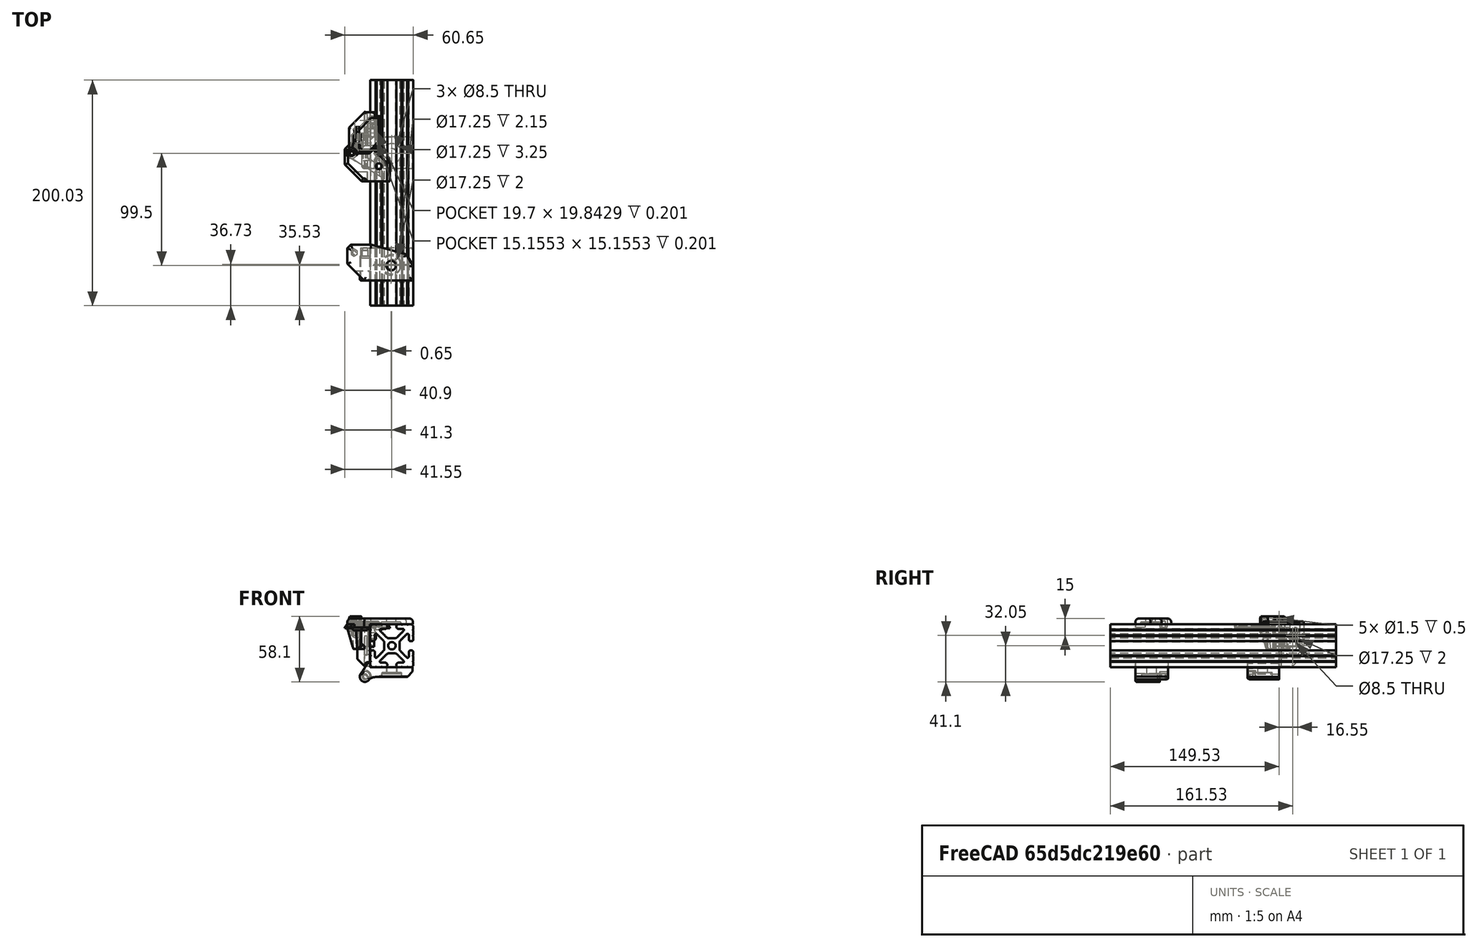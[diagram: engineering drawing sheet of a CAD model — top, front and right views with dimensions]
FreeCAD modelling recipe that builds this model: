
FCSTD DOCUMENT  (FreeCAD 0.18R)
Label: rambo-upper-mount
License: All rights reserved
LicenseURL: http://en.wikipedia.org/wiki/All_rights_reserved
objects: Sketcher::SketchObject×17, PartDesign::Fillet×9, PartDesign::Pad×8, PartDesign::Pocket×7, Part::Feature×6, PartDesign::Body×3, Mesh::Feature×2, PartDesign::Revolution×2, PartDesign::Chamfer×1
note: 70 computed .brp shape members not serialized (recipe doc carries the construction recipe); baked Part::Feature solids carry a one-line shape summary decoded from their .brp

FEATURE [Sketcher::SketchObject] Sketch
  MapMode = 5
  Support = -> [XY_Plane]
  sketch-geometry (7):
    g0: LineSegment StartX=-2.25 StartY=22.75 StartZ=0 EndX=-2.25 EndY=4.5 EndZ=0
    g1: LineSegment StartX=-2.25 StartY=4.5 StartZ=0 EndX=2.25 EndY=0 EndZ=0
    g2: LineSegment StartX=2.25 StartY=0 StartZ=0 EndX=15.7 EndY=0 EndZ=0
    g3: LineSegment StartX=15.7 StartY=0 StartZ=0 EndX=20.5 EndY=4.8 EndZ=0
    g4: LineSegment StartX=20.5 StartY=36.5 StartZ=0 EndX=20.5 EndY=4.8 EndZ=0
    g5: LineSegment StartX=11.5 StartY=36.5 StartZ=0 EndX=20.5 EndY=36.5 EndZ=0
    g6: LineSegment StartX=11.5 StartY=36.5 StartZ=0 EndX=-2.25 EndY=22.75 EndZ=0
  constraints (21):
    c: Coincident(g1,g0)
    c: PointOnObject(g1,g-1)
    c: Coincident(g2,g1)
    c: Horizontal(g2)
    c: Coincident(g4,g3)
    c: Vertical(g4)
    c: Coincident(g5,g4)
    c: Horizontal(g5)
    c: Coincident(g6,g5)
    c: Coincident(g6,g0)
    c: Angle(g1,g0) = 2.35619
    c: Angle(g0,g6) = 2.35619
    c: Angle(g3,g2) = 2.35619
    c: DistanceX(g-1,g5) = 11.5
    c: DistanceY(g-1,g5) = 36.5
    c: DistanceX(g5,g5) = 9
    c: Coincident(g3,g2)
    c: DistanceX(g-1,g2) = 15.7
    c: DistanceX(g-1,g1) = 2.25
    c: Vertical(g0)
    c: DistanceX(g0,g-1) = 2.25
FEATURE [Part::Feature] rambo_base_upper_mount
  shape: bbox 25.4 x 33.05 x 22.5 mm, 98 faces (baked)
  expr: Placement.Base.z = 0
FEATURE [Part::Feature] rambo_base_lower_mount
  shape: bbox 39.91 x 31.71 x 6.307 mm, 79 faces (baked)
FEATURE [Part::Feature] rambo_lid_lower_hinge
  shape: bbox 15.91 x 28.51 x 29.3 mm, 59 faces (baked)
FEATURE [Part::Feature] rambo_base_upper_mount_cs
  shape: bbox 20 x 29.18 x 3e-07 mm, 0 faces, 0 solids (baked)
FEATURE [PartDesign::Pad] Pad
  Length = 2.5
  Length2 = 100
  Profile = -> Sketch
  Type = 0
FEATURE [Sketcher::SketchObject] Sketch001
  AttachmentOffset = pos=(0,0,-14.5) rot=(0,0,1;0rad)
  MapMode = 5
  Placement = pos=(0,14.5,3.2e-15) rot=(1,0,0;1.5708rad)
  Support = -> [XZ_Plane]
  sketch-geometry (5):
    g0: LineSegment StartX=5 StartY=0 StartZ=0 EndX=5 EndY=-30.75 EndZ=0
    g1: LineSegment StartX=5 StartY=-30.75 StartZ=0 EndX=11.25 EndY=-37 EndZ=0
    g2: LineSegment StartX=11.25 StartY=-37 StartZ=0 EndX=16.25 EndY=-37 EndZ=0
    g3: LineSegment StartX=16.25 StartY=-37 StartZ=0 EndX=16.25 EndY=0 EndZ=0
    g4: LineSegment StartX=16.25 StartY=0 StartZ=0 EndX=5 EndY=0 EndZ=0
  constraints (15):
    c: Horizontal(g2)
    c: PointOnObject(g3,g-1)
    c: Vertical(g3)
    c: Angle(g1,g0) = 2.35619
    c: Coincident(g1,g2)
    c: Coincident(g0,g1)
    c: Coincident(g3,g2)
    c: Coincident(g4,g3)
    c: Vertical(g0)
    c: Coincident(g4,g0)
    c: Horizontal(g4)
    c: DistanceX(g-1,g0) = 5
    c: DistanceX(g-1,g3) = 16.25
    c: DistanceY(g2,g-1) = 37
    c: DistanceX(g2,g2) = 5
FEATURE [PartDesign::Pad] Pad001
  BaseFeature = -> Pad
  Length = 2
  Length2 = 100
  Profile = -> Sketch001
  Reversed = true
  Type = 0
FEATURE [Sketcher::SketchObject] Sketch002
  AttachmentOffset = pos=(0,0,16.5) rot=(0,0,1;0rad)
  MapMode = 5
  Placement = pos=(16.5,-3.7e-15,3.7e-15) rot=(0.57735,0.57735,0.57735;2.0944rad)
  Support = -> [YZ_Plane]
  sketch-geometry (6):
    g0: LineSegment StartX=16.5 StartY=0 StartZ=0 EndX=36.5 EndY=0 EndZ=0
    g1: LineSegment StartX=16.5 StartY=0 StartZ=0 EndX=16.5 EndY=-37 EndZ=0
    g2: LineSegment StartX=16.5 StartY=-37 StartZ=0 EndX=26.5 EndY=-37 EndZ=0
    g3: LineSegment StartX=36.5 StartY=0 StartZ=0 EndX=36.5 EndY=-27 EndZ=0
    g4: Circle CenterX=26.5 CenterY=-19.05 CenterZ=0 NormalX=0 NormalY=0 NormalZ=1 AngleXU=0 Radius=4.25
    g5: LineSegment StartX=26.5 StartY=-37 StartZ=0 EndX=36.5 EndY=-27 EndZ=0
  constraints (18):
    c: Coincident(g1,g0)
    c: Vertical(g1)
    c: Horizontal(g2)
    c: DistanceX(g-1,g0) = 16.5
    c: DistanceY(g2,g-1) = 37
    c: Coincident(g2,g1)
    c: Vertical(g3)
    c: Diameter(g4) = 8.5
    c: DistanceY(g4,g-1) = 19.05
    c: Horizontal(g0)
    c: DistanceY(g-1,g0) = 0
    c: DistanceX(g0,g4) = 10
    c: DistanceX(g0,g3) = 20
    c: Coincident(g5,g2)
    c: DistanceX(g2,g5) = 10
    c: Coincident(g5,g3)
    c: Angle(g3,g5) = 2.35619
    c: Coincident(g3,g0)
FEATURE [PartDesign::Pad] Pad002
  BaseFeature = -> Pad001
  Length = 5
  Length2 = 100
  Profile = -> Sketch002
  Reversed = true
  Type = 0
FEATURE [Sketcher::SketchObject] Sketch003
  AttachmentOffset = pos=(0,0,11.5) rot=(0,0,1;0rad)
  MapMode = 5
  Placement = pos=(11.5,-2.6e-15,2.6e-15) rot=(0.57735,0.57735,0.57735;2.0944rad)
  Support = -> [YZ_Plane]
  sketch-geometry (1):
    g0: Circle CenterX=26.5 CenterY=-19.05 CenterZ=0 NormalX=0 NormalY=0 NormalZ=1 AngleXU=0 Radius=8.625
  constraints (3):
    c: Diameter(g0) = 17.25
    c: DistanceY(g0,g-1) = 19.05
    c: DistanceX(g-1,g0) = 26.5
FEATURE [PartDesign::Pocket] Pocket
  BaseFeature = -> Pad002
  Length = 2
  Length2 = 100
  Profile = -> Sketch003
  Reversed = true
  Type = 0
FEATURE [Sketcher::SketchObject] Sketch004
  MapMode = 5
  Support = -> [XY_Plane]
  sketch-geometry (7):
    g0: LineSegment StartX=2.25 StartY=3 StartZ=0 EndX=5.7141 EndY=5 EndZ=0
    g1: LineSegment StartX=5.7141 StartY=5 StartZ=0 EndX=5.7141 EndY=9 EndZ=0
    g2: LineSegment StartX=5.7141 StartY=9 StartZ=0 EndX=2.25 EndY=11 EndZ=0
    g3: LineSegment StartX=2.25 StartY=11 StartZ=0 EndX=-1.2141 EndY=9 EndZ=0
    g4: LineSegment StartX=-1.2141 StartY=9 StartZ=0 EndX=-1.2141 EndY=5 EndZ=0
    g5: LineSegment StartX=-1.2141 StartY=5 StartZ=0 EndX=2.25 EndY=3 EndZ=0
    g6: Circle [constr] CenterX=2.25 CenterY=7 CenterZ=0 NormalX=0 NormalY=0 NormalZ=1 AngleXU=0 Radius=4
  constraints (17):
    c: Coincident(g0,g1)
    c: Coincident(g1,g2)
    c: Coincident(g2,g3)
    c: Coincident(g3,g4)
    c: Coincident(g4,g5)
    c: Coincident(g5,g0)
    c: Equal(g0, g1-g5) x5
    c: PointOnObject(g0,g6)
    c: PointOnObject(g1,g6)
    c: PointOnObject(g2,g6)
    c: PointOnObject(g3,g6)
    c: PointOnObject(g4,g6)
    c: PointOnObject(g5,g6)
    c: DistanceX(g-1,g6) = 2.25
    c: DistanceY(g-1,g6) = 7
    c: Vertical(g1)
    c: DistanceY(g0,g6) = 4
FEATURE [PartDesign::Pad] Pad003
  BaseFeature = -> Pocket
  Length = 3
  Length2 = 100
  Profile = -> Sketch004
  Reversed = true
  Type = 0
FEATURE [Sketcher::SketchObject] Sketch005
  AttachmentOffset = pos=(0,0,-3) rot=(0,0,1;0rad)
  MapMode = 5
  Placement = pos=(0,0,-3) rot=(0,0,1;0rad)
  Support = -> [XY_Plane]
  sketch-geometry (1):
    g0: Circle CenterX=2.25 CenterY=7 CenterZ=0 NormalX=0 NormalY=0 NormalZ=1 AngleXU=0 Radius=1.5
  constraints (3):
    c: Diameter(g0) = 3
    c: DistanceX(g-1,g0) = 2.25
    c: DistanceY(g-1,g0) = 7
FEATURE [PartDesign::Pocket] Pocket001
  BaseFeature = -> Pad003
  Length = 5
  Length2 = 100
  Midplane = true
  Profile = -> Sketch005
  Type = 1
FEATURE [Part::Feature] _515_extrusion_200_25mm_7_7_8in
  Placement = pos=(-110.45,65,-76.25) rot=(1,0,0;1.5708rad)
  shape: bbox 38.1 x 200 x 38.1 mm, 113 faces (baked)
FEATURE [Mesh::Feature] Einsy_base  label="Einsy-base"
  Placement = pos=(16.25,14.5,0) rot=(-0.707107,0.707107,0;3.14159rad)
FEATURE [Part::Feature] rambo_lower_mount
  Placement = pos=(2.25,-88,0) rot=(0,0,1;0rad)
  shape: bbox 58.05 x 31.7 x 8 mm, 46 faces (baked)
FEATURE [PartDesign::Fillet] Fillet
  Base = -> Pocket001 [Face5]
  BaseFeature = -> Pocket001
  Radius = 1.3
FEATURE [PartDesign::Fillet] Fillet001
  Base = -> Fillet [Edge44,Edge46,Edge45]
  BaseFeature = -> Fillet
  Radius = 1
FEATURE [PartDesign::Fillet] Fillet002
  Base = -> Fillet001 [Edge65,Edge102]
  BaseFeature = -> Fillet001
  Radius = 1
FEATURE [PartDesign::Fillet] Fillet003
  Base = -> Fillet002 [Edge83,Edge73,Edge75,Edge77,Edge79,Edge81]
  BaseFeature = -> Fillet002
  Radius = 0.25
FEATURE [PartDesign::Fillet] Fillet004
  Base = -> Fillet003 [Edge40]
  BaseFeature = -> Fillet003
  Radius = 0.35
FEATURE [PartDesign::Body] Body  label="rambo-upper-mount"
  Group = -> [Sketch,Pad,Sketch001,Pad001,Sketch002,Pad002,Sketch003,Pocket,Sketch004,Pad003,Sketch005,Pocket001,Fillet,Fillet001,Fillet002,Fillet003,Fillet004]
  Origin = -> Origin
  Tip = -> Fillet004
FEATURE [Mesh::Feature] Einsy_doors  label="Einsy-doors"
  Placement = pos=(-75.75,14.5,-51) rot=(0,0,1;4.71239rad)
FEATURE [Sketcher::SketchObject] Sketch006
  MapMode = 5
  Support = -> [XY_Plane001]
  sketch-geometry (10):
    g0: LineSegment StartX=0.5 StartY=0.25 StartZ=0 EndX=37.5 EndY=0.25 EndZ=0
    g1: LineSegment StartX=37.5 StartY=0.25 StartZ=0 EndX=37.5 EndY=4.25 EndZ=0
    g2: LineSegment StartX=33.5 StartY=8.5 StartZ=0 EndX=37.5 EndY=4.25 EndZ=0
    g3: LineSegment StartX=-8.36135 StartY=6 StartZ=0 EndX=-1.5 EndY=-4.23326 EndZ=0
    g4: LineSegment StartX=-1 StartY=-4.5 StartZ=0 EndX=0.25 EndY=-4.5 EndZ=0
    g5: LineSegment StartX=33.5 StartY=8.5 StartZ=0 EndX=0.1 EndY=8.5 EndZ=0
    g6: LineSegment StartX=0.25 StartY=-4.5 StartZ=0 EndX=0.25 EndY=0 EndZ=0
    g7: ArcOfCircle CenterX=0.5 CenterY=0 CenterZ=0 NormalX=0 NormalY=0 NormalZ=1 AngleXU=0 Radius=0.25 StartAngle=1.5708 EndAngle=3.14159
    g8: ArcOfCircle CenterX=-4.5 CenterY=8.5 CenterZ=0 NormalX=0 NormalY=0 NormalZ=1 AngleXU=0 Radius=4.6 StartAngle=3.71617 EndAngle=6.28319
    g9: ArcOfCircle CenterX=-1 CenterY=-3.89801 CenterZ=0 NormalX=0 NormalY=0 NormalZ=1 AngleXU=0 Radius=0.601989 StartAngle=3.73224 EndAngle=4.71239
  constraints (29):
    c: Horizontal(g0)
    c: Coincident(g1,g0)
    c: Vertical(g1)
    c: DistanceY(g0,g1) = 4
    c: Coincident(g2,g1)
    c: Horizontal(g5)
    c: Coincident(g5,g2)
    c: DistanceX(g2,g1) = 4
    c: Horizontal(g4)
    c: DistanceX(g-1,g4) = 0.25
    c: Coincident(g6,g4)
    c: Vertical(g6)
    c: Tangent(g0,g7) = 1.5708
    c: Tangent(g6,g7) = 1.5708
    c: DistanceX(g6,g7) = 0.25
    c: PointOnObject(g7,g-1)
    c: Diameter(g8) = 9.2
    c: DistanceX(g8,g-1) = 4.5
    c: DistanceY(g-1,g8) = 8.5
    c: DistanceX(g0,g0) = 37
    c: DistanceY(g6,g6) = 4.5
    c: Tangent(g3,g9) = -1.5708
    c: Tangent(g4,g9) = -1.5708
    c: DistanceX(g3,g9) = 0.5
    c: DistanceX(g4,g4) = 1.25
    c: Coincident(g8,g3)
    c: Coincident(g8,g5)
    c: DistanceY(g-1,g3) = 6
    c: DistanceY(g-1,g5) = 8.5
FEATURE [PartDesign::Pad] Pad004
  Length = 29
  Length2 = 100
  Profile = -> Sketch006
  Reversed = true
  Type = 0
FEATURE [Sketcher::SketchObject] Sketch007
  AttachmentOffset = pos=(-4.5,-9.3,-8.49) rot=(0,1,0;-4.71239rad)
  MapMode = 5
  Placement = pos=(-4.5,8.49,-9.3) rot=(0.57735,0.57735,0.57735;2.0944rad)
  Support = -> [XZ_Plane001]
  sketch-geometry (8):
    g0: LineSegment StartX=-1.75 StartY=9.3 StartZ=0 EndX=0 EndY=9.3 EndZ=0
    g1: LineSegment StartX=-1.75 StartY=9.3 StartZ=0 EndX=-2.5 EndY=7.15 EndZ=0
    g2: LineSegment StartX=-2.5 StartY=7.15 StartZ=0 EndX=-2.5 EndY=2 EndZ=0
    g3: LineSegment StartX=0 StartY=0 StartZ=0 EndX=0 EndY=9.3 EndZ=0
    g4: LineSegment StartX=-2.5 StartY=2 StartZ=0 EndX=-4.6 EndY=2 EndZ=0
    g5: LineSegment StartX=-4.6 StartY=2 StartZ=0 EndX=-4.6 EndY=0 EndZ=0
    g6: LineSegment StartX=-4.6 StartY=0 StartZ=0 EndX=0 EndY=0 EndZ=0
    g7: LineSegment StartX=0 StartY=9.3 StartZ=0 EndX=0 EndY=0 EndZ=0
  constraints (23):
    c: Horizontal(g0)
    c: Coincident(g2,g1)
    c: Vertical(g2)
    c: Coincident(g3,g0)
    c: Vertical(g3)
    c: Coincident(g0,g1)
    c: DistanceX(g0,g0) = 1.75
    c: PointOnObject(g3,g-2)
    c: DistanceX(g1,g3) = 2.5
    c: DistanceY(g1,g0) = 2.15
    c: DistanceY(g2,g1) = 5.15
    c: Coincident(g4,g2)
    c: Horizontal(g4)
    c: DistanceX(g4,g2) = 2.1
    c: Coincident(g5,g4)
    c: PointOnObject(g5,g-1)
    c: Vertical(g5)
    c: Coincident(g6,g5)
    c: Horizontal(g6)
    c: DistanceY(g5,g4) = 2
    c: Coincident(g7,g0)
    c: Coincident(g7,g6)
    c: Coincident(g3,g6)
FEATURE [PartDesign::Revolution] Revolution
  Angle = 360
  Axis = (0,-2e-16,1)
  Base = (-4.5,8.49,-9.3)
  BaseFeature = -> Pad004
  Midplane = true
  Profile = -> Sketch007
  ReferenceAxis = -> Sketch007 [V_Axis]
  Refine = true
FEATURE [Sketcher::SketchObject] Sketch008
  AttachmentOffset = pos=(0,0,-29) rot=(0,0,1;0rad)
  MapMode = 5
  Placement = pos=(0,0,-29) rot=(0,0,1;0rad)
  Support = -> [XY_Plane001]
  sketch-geometry (1):
    g0: Circle CenterX=-4.5 CenterY=8.5 CenterZ=0 NormalX=0 NormalY=0 NormalZ=1 AngleXU=0 Radius=4.6
  constraints (3):
    c: Diameter(g0) = 9.2
    c: DistanceX(g0,g-1) = 4.5
    c: DistanceY(g-1,g0) = 8.5
FEATURE [PartDesign::Pad] Pad005
  BaseFeature = -> Revolution
  Length = 19.7
  Length2 = 100
  Profile = -> Sketch008
  Type = 0
FEATURE [Sketcher::SketchObject] Sketch009
  MapMode = 5
  Support = -> [XY_Plane001]
  sketch-geometry (9):
    g0: ArcOfCircle CenterX=-4.5 CenterY=8.5 CenterZ=0 NormalX=0 NormalY=0 NormalZ=1 AngleXU=0 Radius=4.6 StartAngle=0 EndAngle=0.511093
    g1: Circle [constr] CenterX=-0.487831 CenterY=10.75 CenterZ=0 NormalX=0 NormalY=0 NormalZ=1 AngleXU=0 Radius=0.8
    g2: Circle [constr] CenterX=1.778 CenterY=8.5 CenterZ=0 NormalX=0 NormalY=0 NormalZ=1 AngleXU=0 Radius=0.8
    g3: Circle [constr] CenterX=9.875 CenterY=8.5 CenterZ=0 NormalX=0 NormalY=0 NormalZ=1 AngleXU=0 Radius=0.8
    g4: BSplineCurve PolesCount=3 KnotsCount=2 Degree=2 IsPeriodic=0
    g5: GeomPoint [constr] X=-0.487831 Y=10.75 Z=0
    g6: GeomPoint [constr] X=9.875 Y=8.5 Z=0
    g7: LineSegment StartX=0.1 StartY=8.5 StartZ=0 EndX=1.778 EndY=8.5 EndZ=0
    g8: LineSegment StartX=1.778 StartY=8.5 StartZ=0 EndX=9.875 EndY=8.5 EndZ=0
  constraints (21):
    c: Diameter(g0) = 9.2
    c: DistanceX(g0,g-1) = 4.5
    c: DistanceY(g-1,g0) = 8.5
    c: Radius(g1) = 0.8
    c: Equal(g1,g2)
    c: Equal(g1,g3)
    c: InternalAlignment(g1,g4)
    c: InternalAlignment(g2,g4)
    c: InternalAlignment(g3,g4)
    c: InternalAlignment(g5,g4)
    c: InternalAlignment(g6,g4)
    c: DistanceX(g-1,g4) = 9.875
    c: DistanceY(g4,g2) = 0
    c: Horizontal(g7)
    c: Coincident(g7,g2)
    c: Coincident(g0,g7)
    c: Coincident(g0,g4)
    c: DistanceY(g-1,g4) = 8.5
    c: DistanceY(g0,g0) = 2.25
    c: Coincident(g8,g4)
    c: Horizontal(g8)
FEATURE [PartDesign::Pad] Pad006
  BaseFeature = -> Pad005
  Length = 29
  Length2 = 100
  Profile = -> Sketch009
  Reversed = true
  Type = 0
FEATURE [Sketcher::SketchObject] Sketch010
  MapMode = 5
  Placement = pos=(0,0,0) rot=(1,0,0;1.5708rad)
  Support = -> [XZ_Plane001]
  sketch-geometry (1):
    g0: Circle CenterX=19.05 CenterY=-14.5 CenterZ=0 NormalX=0 NormalY=0 NormalZ=1 AngleXU=0 Radius=4.25
  constraints (3):
    c: Diameter(g0) = 8.5
    c: DistanceX(g-1,g0) = 19.05
    c: DistanceY(g0,g-1) = 14.5
FEATURE [PartDesign::Pocket] Pocket002
  BaseFeature = -> Pad006
  Length = 5
  Length2 = 100
  Profile = -> Sketch010
  Type = 1
FEATURE [Sketcher::SketchObject] Sketch011
  AttachmentOffset = pos=(0,0,-6) rot=(0,0,1;0rad)
  MapMode = 5
  Placement = pos=(0,6,1.3e-15) rot=(1,0,0;1.5708rad)
  Support = -> [XZ_Plane001]
  sketch-geometry (1):
    g0: Circle CenterX=19.05 CenterY=-14.5 CenterZ=0 NormalX=0 NormalY=0 NormalZ=1 AngleXU=0 Radius=8.625
  constraints (3):
    c: Diameter(g0) = 17.25
    c: DistanceX(g-1,g0) = 19.05
    c: DistanceY(g0,g-1) = 14.5
FEATURE [PartDesign::Pocket] Pocket003
  BaseFeature = -> Pocket002
  Length = 5
  Length2 = 100
  Profile = -> Sketch011
  Type = 0
FEATURE [PartDesign::Fillet] Fillet005
  Base = -> Pocket003 [Edge33,Edge58,Edge28,Edge52,Edge27,Edge26,Edge51,Edge15,Edge14,Edge16,Edge56]
  BaseFeature = -> Pocket003
  Radius = 1.3
FEATURE [PartDesign::Fillet] Fillet006
  Base = -> Fillet005 [Edge109]
  BaseFeature = -> Fillet005
  Radius = 0.35
FEATURE [PartDesign::Body] Body001  label="rambo-lower-hinge"
  Group = -> [Sketch006,Pad004,Sketch007,Revolution,Sketch008,Pad005,Sketch009,Pad006,Sketch010,Pocket002,Sketch011,Pocket003,Fillet005,Fillet006]
  Origin = -> Origin001
  Placement = pos=(16.25,-83.8,-38) rot=(-1,0,0;1.5708rad)
  Tip = -> Fillet006
FEATURE [Sketcher::SketchObject] Sketch012
  AttachmentOffset = pos=(16,14.5,-38.1) rot=(1,0,0;-1.5708rad)
  MapMode = 5
  Placement = pos=(16,14.5,-38.1) rot=(1,0,0;4.71239rad)
  Support = -> [XY_Plane002]
  sketch-geometry (11):
    g0: LineSegment StartX=0.5 StartY=0.25 StartZ=0 EndX=37.5 EndY=0.25 EndZ=0
    g1: LineSegment StartX=37.5 StartY=0.25 StartZ=0 EndX=37.5 EndY=4.25 EndZ=0
    g2: LineSegment StartX=33.5 StartY=8.5 StartZ=0 EndX=37.5 EndY=4.25 EndZ=0
    g3: LineSegment StartX=-2.71273 StartY=-4.5 StartZ=0 EndX=0.25 EndY=-4.5 EndZ=0
    g4: LineSegment StartX=33.5 StartY=8.5 StartZ=0 EndX=-1.752 EndY=8.5 EndZ=0
    g5: LineSegment StartX=0.25 StartY=-4.5 StartZ=0 EndX=0.25 EndY=0 EndZ=0
    g6: ArcOfCircle CenterX=0.5 CenterY=0 CenterZ=0 NormalX=0 NormalY=0 NormalZ=1 AngleXU=0 Radius=0.25 StartAngle=1.5708 EndAngle=3.14159
    g7: LineSegment StartX=-5.87481 StartY=6.5 StartZ=0 EndX=-4.064 EndY=1.4 EndZ=0
    g8: LineSegment StartX=-4.064 StartY=1.4 StartZ=0 EndX=-4.064 EndY=-3.14873 EndZ=0
    g9: LineSegment StartX=-4.064 StartY=-3.14873 StartZ=0 EndX=-2.71273 EndY=-4.5 EndZ=0
    g10: ArcOfCircle CenterX=-4.25 CenterY=8.4 CenterZ=0 NormalX=0 NormalY=0 NormalZ=1 AngleXU=0 Radius=2.5 StartAngle=0.0400107 EndAngle=4.00491
  constraints (28):
    c: Horizontal(g0)
    c: Coincident(g1,g0)
    c: Vertical(g1)
    c: DistanceY(g0,g1) = 4
    c: Coincident(g2,g1)
    c: Horizontal(g4)
    c: Coincident(g4,g2)
    c: DistanceX(g2,g1) = 4
    c: Horizontal(g3)
    c: Coincident(g5,g3)
    c: Vertical(g5)
    c: Tangent(g0,g6) = 1.5708
    c: Tangent(g5,g6) = 1.5708
    c: DistanceX(g5,g6) = 0.25
    c: PointOnObject(g6,g-1)
    c: DistanceX(g0,g0) = 37
    c: DistanceY(g5,g5) = 4.5
    c: Vertical(g8)
    c: Coincident(g9,g3)
    c: Coincident(g9,g8)
    c: Coincident(g8,g7)
    c: Angle(g9,g8) = 2.35619
    c: Diameter(g10) = 5
    c: DistanceX(g10,g-1) = 4.25
    c: DistanceY(g-1,g10) = 8.4
    c: DistanceY(g-1,g7) = 1.4
    c: Coincident(g10,g4)
    c: Coincident(g10,g7)
FEATURE [PartDesign::Pad] Pad007
  Length = 28
  Length2 = 100
  Profile = -> Sketch012
  Reversed = true
  Type = 0
FEATURE [Sketcher::SketchObject] Sketch013
  AttachmentOffset = pos=(0,0,6.5) rot=(0,0,1;0rad)
  MapMode = 5
  Placement = pos=(0,-6.5,-1.4e-15) rot=(1,0,0;1.5708rad)
  Support = -> [XZ_Plane002]
  sketch-geometry (1):
    g0: Circle CenterX=11.75 CenterY=-46.5 CenterZ=0 NormalX=0 NormalY=0 NormalZ=1 AngleXU=0 Radius=4.625
  constraints (3):
    c: Diameter(g0) = 9.25
    c: DistanceX(g-1,g0) = 11.75
    c: DistanceY(g0,g-1) = 46.5
FEATURE [PartDesign::Pocket] Pocket004
  BaseFeature = -> Pad007
  Length = 7
  Length2 = 100
  Profile = -> Sketch013
  Reversed = true
  Type = 0
FEATURE [Sketcher::SketchObject] Sketch014
  AttachmentOffset = pos=(-6.5,-46.5,11.75) rot=(0,0,1;0rad)
  MapMode = 5
  Placement = pos=(11.75,-6.5,-46.5) rot=(0.57735,0.57735,0.57735;2.0944rad)
  Support = -> [YZ_Plane002]
  sketch-geometry (5):
    g0: LineSegment StartX=-6.73205 StartY=1.5 StartZ=0 EndX=-6.73205 EndY=0 EndZ=0
    g1: LineSegment StartX=-5 StartY=2.5 StartZ=0 EndX=0 EndY=2.5 EndZ=0
    g2: LineSegment StartX=0 StartY=2.5 StartZ=0 EndX=0 EndY=0 EndZ=0
    g3: LineSegment StartX=-6.73205 StartY=0 StartZ=0 EndX=0 EndY=0 EndZ=0
    g4: LineSegment StartX=-6.73205 StartY=1.5 StartZ=0 EndX=-5 EndY=2.5 EndZ=0
  constraints (14):
    c: Vertical(g0)
    c: Horizontal(g1)
    c: Coincident(g2,g1)
    c: Vertical(g2)
    c: Coincident(g3,g2)
    c: Horizontal(g3)
    c: Coincident(g0,g3)
    c: DistanceY(g2,g2) = 2.5
    c: Coincident(g4,g0)
    c: Coincident(g4,g1)
    c: DistanceY(g0,g0) = 1.5
    c: DistanceX(g1,g1) = 5
    c: Angle(g0,g4) = 2.0944
    c: Coincident(g2,g-1)
FEATURE [PartDesign::Revolution] Revolution001
  Angle = 360
  Axis = (3e-16,1,-2e-16)
  Base = (11.75,-6.5,-46.5)
  BaseFeature = -> Pocket004
  Profile = -> Sketch014
  ReferenceAxis = -> Sketch014 [H_Axis]
FEATURE [Sketcher::SketchObject] Sketch015
  MapMode = 5
  Support = -> [XY_Plane002]
  sketch-geometry (1):
    g0: Circle CenterX=35.55 CenterY=0 CenterZ=0 NormalX=0 NormalY=0 NormalZ=1 AngleXU=0 Radius=4.25
  constraints (3):
    c: Diameter(g0) = 8.5
    c: PointOnObject(g0,g-1)
    c: DistanceX(g-1,g0) = 35.55
FEATURE [PartDesign::Pocket] Pocket005
  BaseFeature = -> Revolution001
  Length = 5
  Length2 = 100
  Profile = -> Sketch015
  Type = 1
FEATURE [Sketcher::SketchObject] Sketch016
  AttachmentOffset = pos=(0,0,-43) rot=(0,0,1;0rad)
  MapMode = 5
  Placement = pos=(0,0,-43) rot=(0,0,1;0rad)
  Support = -> [XY_Plane002]
  sketch-geometry (1):
    g0: Circle CenterX=35.55 CenterY=0 CenterZ=0 NormalX=0 NormalY=0 NormalZ=1 AngleXU=0 Radius=8.625
  constraints (3):
    c: Diameter(g0) = 17.25
    c: PointOnObject(g0,g-1)
    c: DistanceX(g-1,g0) = 35.55
FEATURE [PartDesign::Pocket] Pocket006
  BaseFeature = -> Pocket005
  Length = 4
  Length2 = 100
  Profile = -> Sketch016
  Type = 0
FEATURE [PartDesign::Chamfer] Chamfer
  Base = -> Pocket006 [Edge23,Edge40]
  BaseFeature = -> Pocket006
  Size = 1
FEATURE [PartDesign::Fillet] Fillet007
  Base = -> Chamfer [Edge6,Edge8,Edge10,Edge42,Edge37,Edge38,Edge29,Edge31,Edge49]
  BaseFeature = -> Chamfer
  Radius = 0.25
FEATURE [PartDesign::Fillet] Fillet008
  Base = -> Fillet007 [Edge61]
  BaseFeature = -> Fillet007
  Radius = 0.35
FEATURE [PartDesign::Body] Body002  label="rambo-upper-hinge"
  Group = -> [Sketch012,Pad007,Sketch013,Pocket004,Sketch014,Revolution001,Sketch015,Pocket005,Sketch016,Pocket006,Chamfer,Fillet007,Fillet008]
  Origin = -> Origin002
  Tip = -> Fillet008
